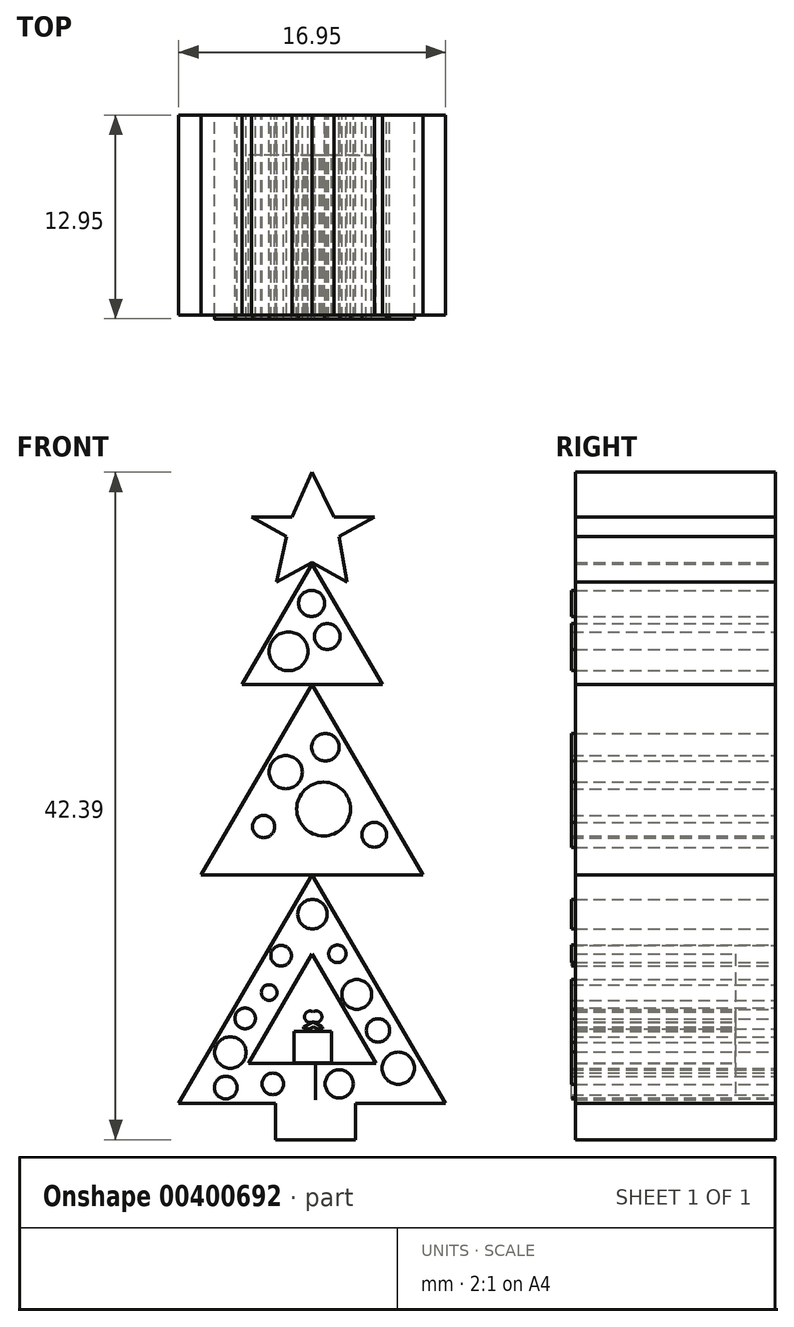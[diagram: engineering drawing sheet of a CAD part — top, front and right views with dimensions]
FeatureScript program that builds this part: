
annotation { "Feature Type Name" : "Feature", "Feature Type Description" : "" }
export const myFeature = defineFeature(function(context is Context, id is Id, definition is map)
    precondition{}
    {
        {
            var Q0;
            Q0=qCreatedBy(makeId("Front.planeOp"),FACE);
            var sketch = newSketch(context, id + "F0", { "sketchPlane" : qUnion([Q0])});
            skLineSegment(sketch, "E0", {"start": v(35.06, 50.68) * mm, "end": v(30.6, 43.03) * mm});
            skLineSegment(sketch, "E1", {"start": v(30.6, 43.03) * mm, "end": v(35.06, 50.68) * mm});
            skLineSegment(sketch, "E2", {"start": v(35.06, 50.68) * mm, "end": v(39.53, 43.03) * mm});
            skLineSegment(sketch, "E3", {"start": v(39.53, 43.03) * mm, "end": v(30.6, 43.03) * mm});
            skLineSegment(sketch, "E4", {"start": v(35.06, 43.03) * mm, "end": v(28.02, 30.96) * mm});
            skLineSegment(sketch, "E5", {"start": v(28.02, 30.96) * mm, "end": v(35.06, 43.03) * mm});
            skLineSegment(sketch, "E6", {"start": v(35.06, 43.03) * mm, "end": v(42.1, 30.96) * mm});
            skLineSegment(sketch, "E7", {"start": v(42.1, 30.96) * mm, "end": v(28.02, 30.96) * mm});
            skLineSegment(sketch, "E8", {"start": v(35.06, 30.96) * mm, "end": v(26.59, 16.42) * mm});
            skLineSegment(sketch, "E9", {"start": v(26.59, 16.42) * mm, "end": v(35.06, 30.96) * mm});
            skLineSegment(sketch, "E10", {"start": v(35.06, 30.96) * mm, "end": v(43.54, 16.42) * mm});
            skLineSegment(sketch, "E11", {"start": v(43.54, 16.42) * mm, "end": v(26.59, 16.42) * mm});
            skLineSegment(sketch, "E12.bottom", {"start": v(32.73, 16.42) * mm, "end": v(37.83, 16.42) * mm});
            skLineSegment(sketch, "E12.top", {"start": v(32.73, 14.13) * mm, "end": v(37.83, 14.13) * mm});
            skLineSegment(sketch, "E12.left", {"start": v(32.73, 16.42) * mm, "end": v(32.73, 14.13) * mm});
            skLineSegment(sketch, "E12.right", {"start": v(37.83, 16.42) * mm, "end": v(37.83, 14.13) * mm});
            skSolve(sketch);
        }
        {
            var Q0;
            Q0 = qSketchRegion(id + "F0", true);
            extrude(context, id + "F1", {"entities" : qUnion([Q0]), "depth" : 12.7 * mm});
        }
        {
            var Q0;
            Q0=qCreatedBy(makeId("Front.planeOp"),FACE);
            var sketch = newSketch(context, id + "F2", { "sketchPlane" : qUnion([Q0])});
            skLineSegment(sketch, "E13", {"start": v(35.06, 50.78) * mm, "end": v(37.27, 49.54) * mm});
            skLineSegment(sketch, "E14", {"start": v(37.27, 49.54) * mm, "end": v(36.78, 52.43) * mm});
            skLineSegment(sketch, "E15", {"start": v(36.78, 52.43) * mm, "end": v(39.04, 53.67) * mm});
            skLineSegment(sketch, "E16", {"start": v(35.06, 50.78) * mm, "end": v(32.8, 49.54) * mm});
            skLineSegment(sketch, "E17", {"start": v(32.8, 49.54) * mm, "end": v(33.44, 52.43) * mm});
            skLineSegment(sketch, "E18", {"start": v(33.44, 52.43) * mm, "end": v(31.22, 53.67) * mm});
            skLineSegment(sketch, "E19", {"start": v(31.22, 53.67) * mm, "end": v(33.78, 53.67) * mm});
            skLineSegment(sketch, "E20", {"start": v(39.04, 53.67) * mm, "end": v(36.45, 53.67) * mm});
            skLineSegment(sketch, "E21", {"start": v(36.45, 53.67) * mm, "end": v(35.06, 56.52) * mm});
            skLineSegment(sketch, "E22", {"start": v(35.06, 56.52) * mm, "end": v(33.78, 53.67) * mm});
            skSolve(sketch);
        }
        {
            var Q0;
            Q0 = qSketchRegion(id + "F2", true);
            extrude(context, id + "F3", {"entities" : qUnion([Q0]), "depth" : 12.7 * mm});
        }
        {
            var Q0;
            Q0=makeQuery(id+"F1.opExtrude","CAP_FACE",FACE,{"disambiguationData":[OSD([sQuery(id+"F0.wireOp",EDGE,"E9"),sQuery(id+"F0.wireOp",EDGE,"E10"),sQuery(id+"F0.wireOp",EDGE,"E11"),sQuery(id+"F0.wireOp",EDGE,"E12.top"),sQuery(id+"F0.wireOp",EDGE,"E12.left"),sQuery(id+"F0.wireOp",EDGE,"E12.right")])],"isStart":false});
            shell(context, id + "F4", {"entities" : qUnion([Q0]), "thickness" : 2.54 * mm});
        }
        {
            var Q0;
            Q0=qCreatedBy(makeId("Front.planeOp"),FACE);
            var sketch = newSketch(context, id + "F5", { "sketchPlane" : qUnion([Q0])});
            skLineSegment(sketch, "E23.bottom", {"start": v(33.92, 21) * mm, "end": v(36.28, 21) * mm});
            skLineSegment(sketch, "E23.top", {"start": v(33.92, 19.01) * mm, "end": v(36.28, 19.01) * mm});
            skLineSegment(sketch, "E23.left", {"start": v(33.92, 21) * mm, "end": v(33.92, 19.01) * mm});
            skLineSegment(sketch, "E23.right", {"start": v(36.28, 21) * mm, "end": v(36.28, 19.01) * mm});
            skSolve(sketch);
        }
        {
            var Q0;
            Q0 = qSketchRegion(id + "F5", true);
            extrude(context, id + "F6", {"entities" : qUnion([Q0]), "operationType" : NewBodyOperationType.ADD, "depth" : 12.7 * mm});
        }
        {
            var Q0;
            Q0=qCreatedBy(makeId("Front.planeOp"),FACE);
            var sketch = newSketch(context, id + "F7", { "sketchPlane" : qUnion([Q0])});
            skLineSegment(sketch, "E24", {"start": v(35.14, 21.3) * mm, "end": v(35.64, 21.05) * mm});
            skLineSegment(sketch, "E25", {"start": v(35.64, 21.05) * mm, "end": v(35.14, 21.3) * mm});
            skLineSegment(sketch, "E26", {"start": v(35.14, 21.3) * mm, "end": v(34.64, 21.05) * mm});
            skLineSegment(sketch, "E27", {"start": v(34.64, 21.05) * mm, "end": v(34.76, 21.3) * mm});
            skLineSegment(sketch, "E28", {"start": v(34.76, 21.3) * mm, "end": v(34.64, 21.05) * mm});
            skLineSegment(sketch, "E29", {"start": v(35.64, 21.05) * mm, "end": v(35.52, 21.3) * mm});
            skLineSegment(sketch, "E30", {"start": v(35.52, 21.3) * mm, "end": v(35.76, 21.18) * mm});
            skLineSegment(sketch, "E31", {"start": v(35.76, 21.18) * mm, "end": v(35.52, 21.3) * mm});
            skLineSegment(sketch, "E32", {"start": v(34.76, 21.3) * mm, "end": v(34.52, 21.18) * mm});
            skLineSegment(sketch, "E33", {"start": v(34.52, 21.18) * mm, "end": v(34.52, 21.3) * mm});
            skLineSegment(sketch, "E34", {"start": v(34.52, 21.3) * mm, "end": v(35.14, 21.6) * mm});
            skLineSegment(sketch, "E35", {"start": v(35.14, 21.6) * mm, "end": v(34.52, 21.3) * mm});
            skLineSegment(sketch, "E36", {"start": v(35.76, 21.18) * mm, "end": v(35.7, 21.3) * mm});
            skLineSegment(sketch, "E37", {"start": v(35.7, 21.3) * mm, "end": v(35.14, 21.6) * mm});
            skSolve(sketch);
        }
        {
            var Q0;
            Q0=qCreatedBy(makeId("Front.planeOp"),FACE);
            var sketch = newSketch(context, id + "F8", { "sketchPlane" : qUnion([Q0])});
            skCircle(sketch, "E38", {"center": v(35.31, 21.94) * mm, "radius": 0.37 * mm});
            skCircle(sketch, "E39", {"center": v(34.94, 21.94) * mm, "radius": 0.37 * mm});
            skSolve(sketch);
        }
        {
            var Q0;
            Q0 = qSketchRegion(id + "F8", true);
            var Q1;
            Q1 = qSketchRegion(id + "F7", true);
            extrude(context, id + "F9", {"entities" : qUnion([Q0, Q1]), "operationType" : NewBodyOperationType.ADD, "depth" : 12.7 * mm});
        }
        {
            var Q0;
            Q0=qCreatedBy(makeId("Front.planeOp"),FACE);
            var sketch = newSketch(context, id + "F10", { "sketchPlane" : qUnion([Q0])});
            skCircle(sketch, "E40", {"center": v(35.03, 48.2) * mm, "radius": 0.83 * mm});
            skCircle(sketch, "E41", {"center": v(36.02, 46.09) * mm, "radius": 0.82 * mm});
            skCircle(sketch, "E42", {"center": v(33.56, 45.15) * mm, "radius": 1.23 * mm});
            skCircle(sketch, "E43", {"center": v(35.9, 39.06) * mm, "radius": 0.87 * mm});
            skCircle(sketch, "E44", {"center": v(33.39, 37.48) * mm, "radius": 1.06 * mm});
            skCircle(sketch, "E45", {"center": v(35.79, 35.13) * mm, "radius": 1.7 * mm});
            skCircle(sketch, "E46", {"center": v(31.98, 34.02) * mm, "radius": 0.7 * mm});
            skCircle(sketch, "E47", {"center": v(39.01, 33.5) * mm, "radius": 0.79 * mm});
            skCircle(sketch, "E48", {"center": v(35.08, 28.45) * mm, "radius": 0.94 * mm});
            skCircle(sketch, "E49", {"center": v(36.67, 25.93) * mm, "radius": 0.56 * mm});
            skCircle(sketch, "E50", {"center": v(37.9, 23.36) * mm, "radius": 0.94 * mm});
            skCircle(sketch, "E51", {"center": v(40.53, 18.67) * mm, "radius": 1.02 * mm});
            skCircle(sketch, "E52", {"center": v(39.24, 21.07) * mm, "radius": 0.75 * mm});
            skCircle(sketch, "E53", {"center": v(36.78, 17.67) * mm, "radius": 0.9 * mm});
            skCircle(sketch, "E54", {"center": v(33.1, 25.82) * mm, "radius": 0.66 * mm});
            skCircle(sketch, "E55", {"center": v(32.33, 23.47) * mm, "radius": 0.5 * mm});
            skCircle(sketch, "E56", {"center": v(30.8, 21.83) * mm, "radius": 0.66 * mm});
            skCircle(sketch, "E57", {"center": v(29.87, 19.66) * mm, "radius": 1 * mm});
            skCircle(sketch, "E58", {"center": v(29.58, 17.44) * mm, "radius": 0.72 * mm});
            skCircle(sketch, "E59", {"center": v(32.57, 17.67) * mm, "radius": 0.69 * mm});
            skSolve(sketch);
        }
        {
            var Q0;
            Q0 = qSketchRegion(id + "F10", true);
            extrude(context, id + "F11", {"entities" : qUnion([Q0]), "depth" : 12.95 * mm});
        }
    });
